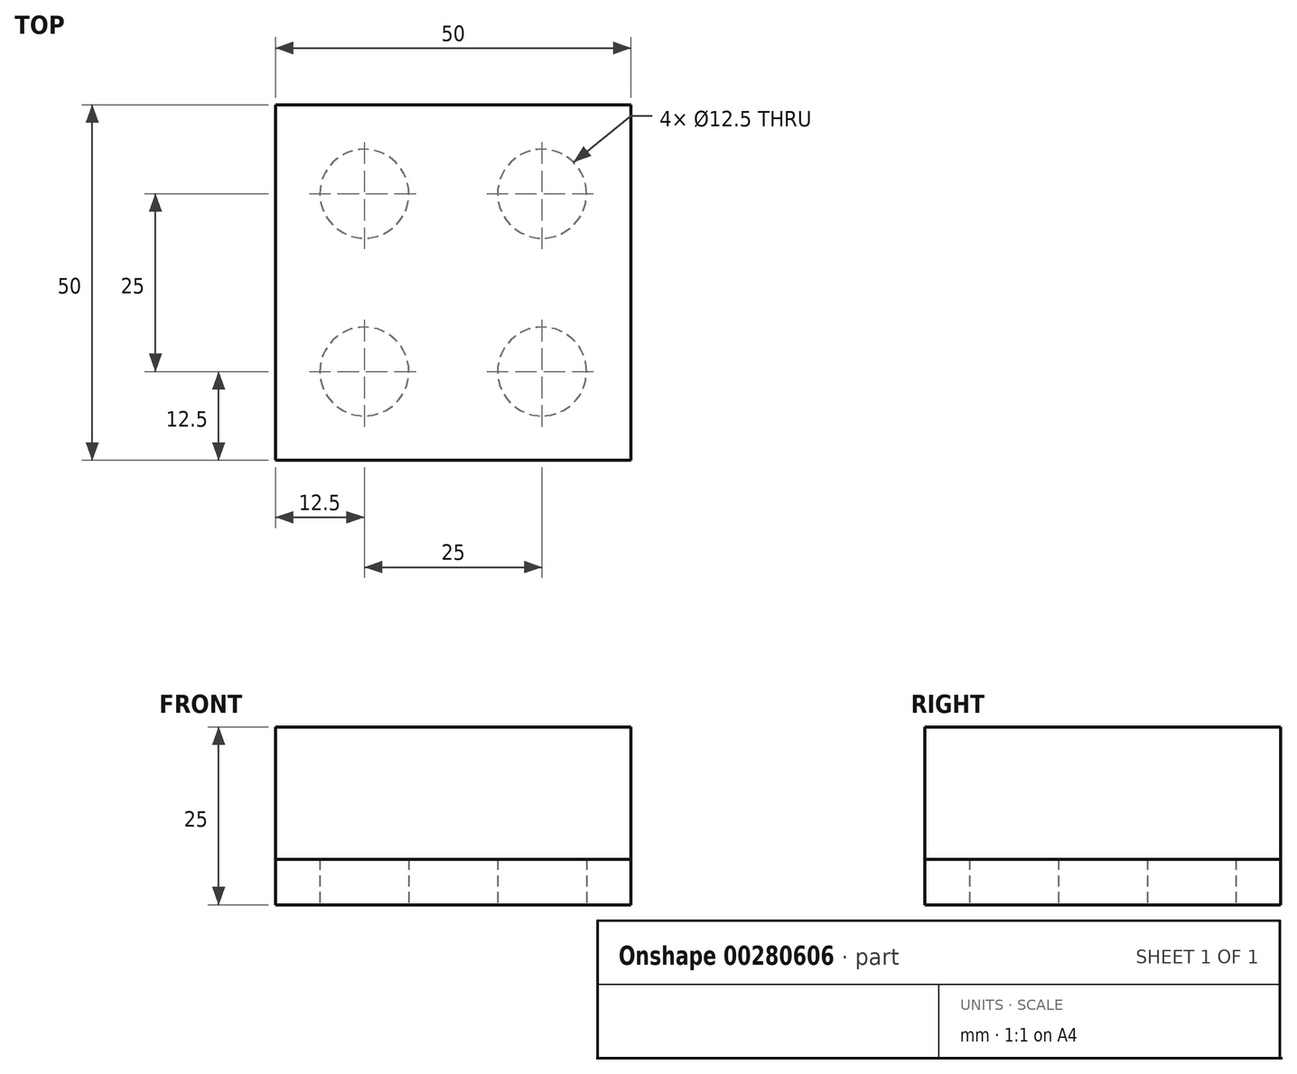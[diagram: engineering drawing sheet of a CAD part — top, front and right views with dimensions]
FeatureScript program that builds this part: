
annotation { "Feature Type Name" : "Feature", "Feature Type Description" : "" }
export const myFeature = defineFeature(function(context is Context, id is Id, definition is map)
    precondition{}
    {
        {
            assignVariable(context, id + "F0", {"name" : "Thickness", "anyValue" : 6.4 * mm});
        }
        {
            var Q0;
            Q0=qCreatedBy(makeId("Top.planeOp"),FACE);
            var sketch = newSketch(context, id + "F1", { "sketchPlane" : qUnion([Q0])});
            skLineSegment(sketch, "E0.bottom", {"start": v(25, 25) * mm, "end": v(-25, 25) * mm});
            skLineSegment(sketch, "E0.top", {"start": v(25, -25) * mm, "end": v(-25, -25) * mm});
            skLineSegment(sketch, "E0.left", {"start": v(25, 25) * mm, "end": v(25, -25) * mm});
            skLineSegment(sketch, "E0.right", {"start": v(-25, 25) * mm, "end": v(-25, -25) * mm});
            skPoint(sketch, "E0.middle", {"position": v(0, 0) * mm});
            skCircle(sketch, "E1", {"center": v(-12.5, 12.5) * mm, "radius": 6.25 * mm});
            skCircle(sketch, "E2", {"center": v(12.5, 12.5) * mm, "radius": 6.25 * mm});
            skCircle(sketch, "E3", {"center": v(12.5, -12.5) * mm, "radius": 6.25 * mm});
            skCircle(sketch, "E4", {"center": v(-12.5, -12.5) * mm, "radius": 6.25 * mm});
            skLineSegment(sketch, "E5", {"start": v(-25, 0) * mm, "end": v(25, 0) * mm, "construction": true});
            skLineSegment(sketch, "E6", {"start": v(0, -25) * mm, "end": v(0, 25) * mm, "construction": true});
            skLineSegment(sketch, "E7", {"start": v(-25, 25) * mm, "end": v(0, 25) * mm});
            skLineSegment(sketch, "E8", {"start": v(0, 25) * mm, "end": v(25, 25) * mm});
            skLineSegment(sketch, "E9", {"start": v(25, 25) * mm, "end": v(25, 0) * mm});
            skLineSegment(sketch, "E10", {"start": v(25, 0) * mm, "end": v(25, -25) * mm});
            skLineSegment(sketch, "E11", {"start": v(25, -25) * mm, "end": v(0, -25) * mm});
            skLineSegment(sketch, "E12", {"start": v(0, -25) * mm, "end": v(-25, -25) * mm});
            skLineSegment(sketch, "E13", {"start": v(-25, -25) * mm, "end": v(-25, 0) * mm});
            skLineSegment(sketch, "E14", {"start": v(-25, 0) * mm, "end": v(-25, 25) * mm});
            skLineSegment(sketch, "E15", {"start": v(-25, 12.5) * mm, "end": v(25, 12.5) * mm, "construction": true});
            skLineSegment(sketch, "E16", {"start": v(12.5, -25) * mm, "end": v(12.5, 25) * mm, "construction": true});
            skLineSegment(sketch, "E17", {"start": v(-12.5, -25) * mm, "end": v(-12.5, 25) * mm, "construction": true});
            skLineSegment(sketch, "E18", {"start": v(-25, -12.5) * mm, "end": v(25, -12.5) * mm, "construction": true});
            skLineSegment(sketch, "E19", {"start": v(0, 12.5) * mm, "end": v(12.5, 12.5) * mm, "construction": true});
            skPoint(sketch, "E20", {"position": v(6.25, 12.5) * mm});
            skSolve(sketch);
        }
        {
            var Q0;
            Q0 = qSketchRegion(id + "F1", true);
            extrude(context, id + "F2", {"entities" : qUnion([Q0]), "depth" : getVariable(context, 'Thickness')});
        }
        {
            var Q0;
            Q0=makeQuery(id+"F1.imprint","IMPRINT",FACE,{"disambiguationData":[TD([[makeQuery(id+"F1.imprint","IMPRINT",EDGE,{"derivedFrom":sQuery(id+"F1.wireOp",EDGE,"E1")}),-1.0]])]});
            var Q1;
            Q1=makeQuery(id+"F1.imprint","IMPRINT",FACE,{"disambiguationData":[TD([[makeQuery(id+"F1.imprint","IMPRINT",EDGE,{"derivedFrom":sQuery(id+"F1.wireOp",EDGE,"E4")}),1.0]])]});
            var Q2;
            Q2=makeQuery(id+"F1.imprint","IMPRINT",FACE,{"disambiguationData":[TD([[makeQuery(id+"F1.imprint","IMPRINT",EDGE,{"derivedFrom":sQuery(id+"F1.wireOp",EDGE,"E3")}),1.0]])]});
            var Q3;
            Q3=makeQuery(id+"F1.imprint","IMPRINT",FACE,{"disambiguationData":[TD([[makeQuery(id+"F1.imprint","IMPRINT",EDGE,{"derivedFrom":sQuery(id+"F1.wireOp",EDGE,"E2")}),1.0]])]});
            var Q4;
            Q4=makeQuery(id+"F1.imprint","IMPRINT",FACE,{"disambiguationData":[TD([[makeQuery(id+"F1.imprint","IMPRINT",EDGE,{"derivedFrom":sQuery(id+"F1.wireOp",EDGE,"E1")}),1.0]])]});
            extrude(context, id + "F3", {"entities" : qUnion([Q0, Q1, Q2, Q3, Q4]), "depth" : 25 * mm});
        }
    });
